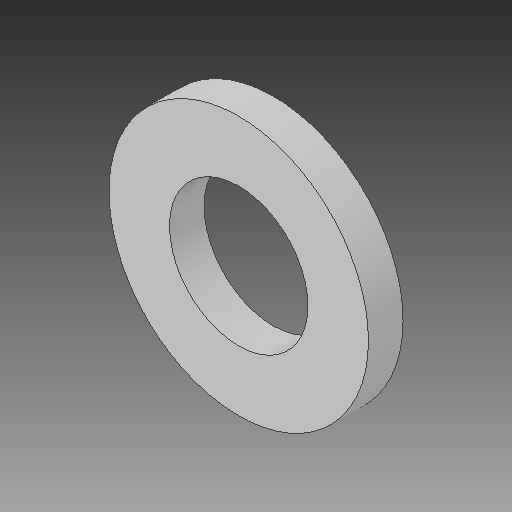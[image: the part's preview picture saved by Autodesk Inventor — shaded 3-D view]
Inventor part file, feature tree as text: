
AUTODESK INVENTOR PART (.ipt)
format: ipt  version: 2018 (Build 220112000, 112)  size: 94,208 bytes
history: native  units: mm
features: other x3, sketch x1
ambient origin geometry x8: Origin, YZ Plane, XZ Plane, XY Plane, X Axis, Y Axis, Z Axis, Center Point
bodies: Solid1 (feature_tree)
feature tree (4):
  other  "M3 Washer.ipt"
  other  "Solid1::M3 Washer.ipt"
  other  "TaggingFeature1"
  sketch  "Sketch1"  dims[d0=10.0mm]
